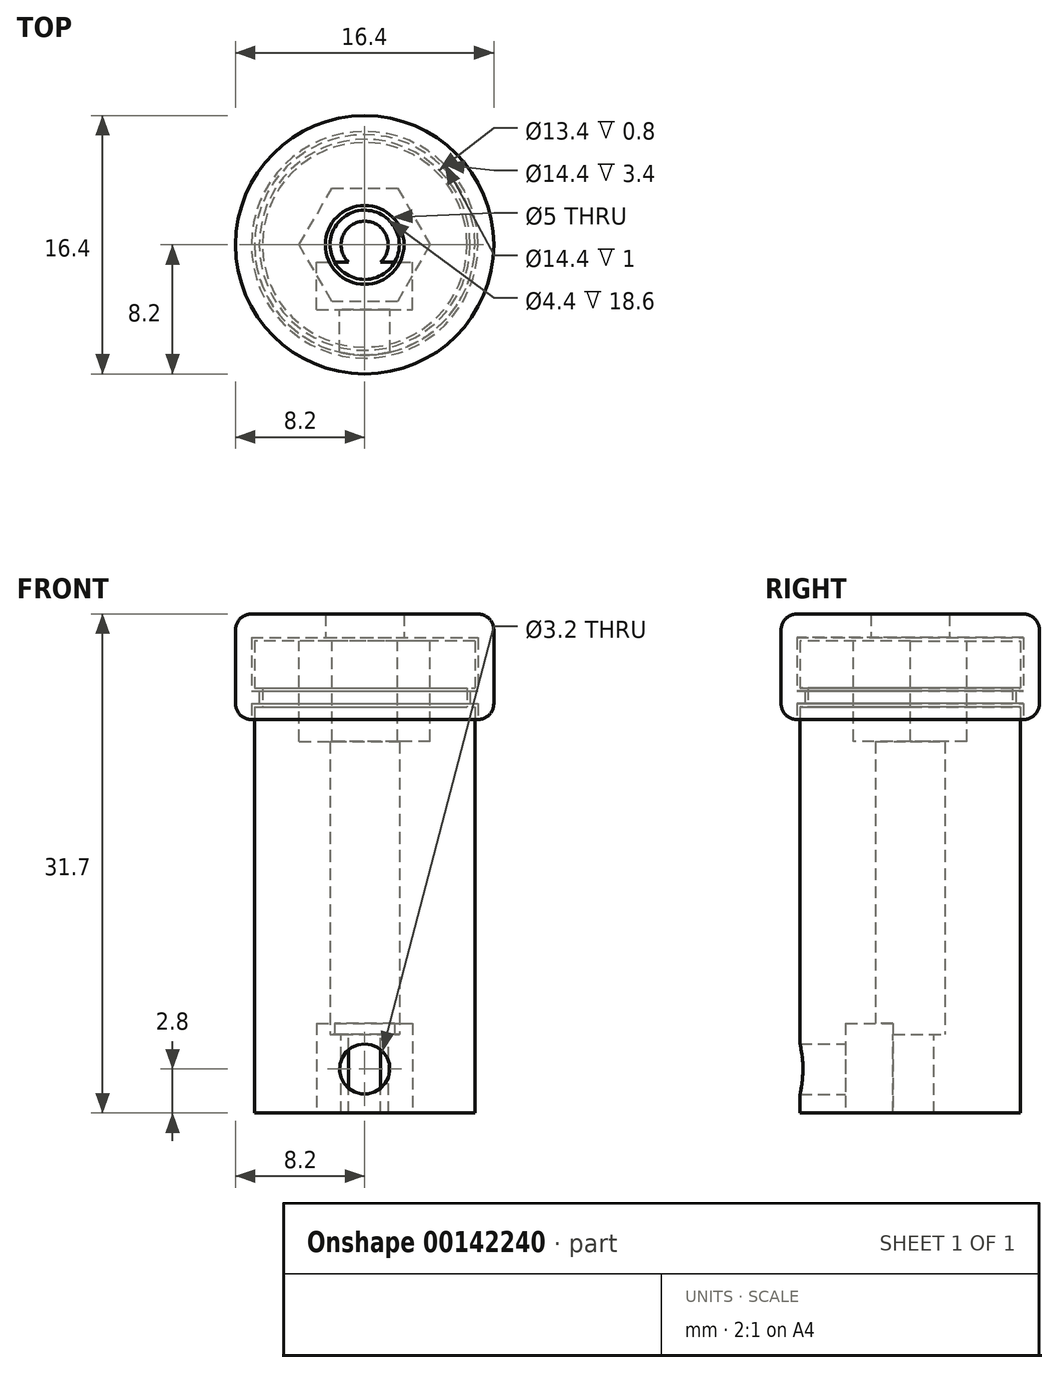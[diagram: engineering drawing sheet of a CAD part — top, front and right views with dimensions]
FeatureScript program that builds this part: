
annotation { "Feature Type Name" : "Feature", "Feature Type Description" : "" }
export const myFeature = defineFeature(function(context is Context, id is Id, definition is map)
    precondition{}
    {
        {
            var Q0;
            Q0=qCreatedBy(makeId("Top.planeOp"),FACE);
            var sketch = newSketch(context, id + "F0", { "sketchPlane" : qUnion([Q0])});
            skCircle(sketch, "E0", {"center": v(0, 0) * mm, "radius": 2.2 * mm});
            skCircle(sketch, "E1", {"center": v(0, 0) * mm, "radius": 7 * mm});
            skSolve(sketch);
        }
        {
            var Q0;
            Q0=makeQuery(id+"F0.imprint","IMPRINT",FACE,{"disambiguationData":[TD([[makeQuery(id+"F0.imprint","IMPRINT",EDGE,{"derivedFrom":sQuery(id+"F0.wireOp",EDGE,"E0")}),-1.0]])]});
            extrude(context, id + "F1", {"entities" : qUnion([Q0]), "depth" : 25 * mm});
        }
        {
            var Q0;
            Q0=makeQuery(id+"F1.opExtrude","CAP_FACE",FACE,{"disambiguationData":[OSD([sQuery(id+"F0.wireOp",EDGE,"E0"),sQuery(id+"F0.wireOp",EDGE,"E1")])],"isStart":false});
            var sketch = newSketch(context, id + "F2", { "sketchPlane" : qUnion([Q0])});
            skCircle(sketch, "E2.cCircle", {"center": v(0, 0) * mm, "radius": 3.6 * mm, "construction": true});
            skLineSegment(sketch, "E2.0", {"start": v(2.08, -3.6) * mm, "end": v(-2.08, -3.6) * mm});
            skLineSegment(sketch, "E2.1", {"start": v(-2.08, -3.6) * mm, "end": v(-4.16, 0) * mm});
            skLineSegment(sketch, "E2.2", {"start": v(-4.16, 0) * mm, "end": v(-2.08, 3.6) * mm});
            skLineSegment(sketch, "E2.3", {"start": v(-2.08, 3.6) * mm, "end": v(2.08, 3.6) * mm});
            skLineSegment(sketch, "E2.4", {"start": v(2.08, 3.6) * mm, "end": v(4.16, 0) * mm});
            skLineSegment(sketch, "E2.5", {"start": v(4.16, 0) * mm, "end": v(2.08, -3.6) * mm});
            skPoint(sketch, "E2.0.midPoint", {"position": v(0, -3.6) * mm});
            skSolve(sketch);
        }
        {
            var Q0;
            Q0=makeQuery(id+"F2.imprint","IMPRINT",FACE,{"disambiguationData":[TD([[makeQuery(id+"F2.imprint","IMPRINT",EDGE,{"derivedFrom":makeQuery(id+"F1.opExtrude","CAP_EDGE",EDGE,{"disambiguationData":[OSD([sQuery(id+"F0.wireOp",EDGE,"E0")])],"isStart":false})}),1.0]])]});
            var Q1;
            Q1=makeQuery(id+"F2.imprint","IMPRINT",FACE,{"disambiguationData":[TD([[makeQuery(id+"F2.imprint","IMPRINT",EDGE,{"derivedFrom":sQuery(id+"F2.wireOp",EDGE,"E2.0")}),-1.0]])]});
            extrude(context, id + "F3", {"entities" : qUnion([Q0, Q1]), "operationType" : NewBodyOperationType.REMOVE, "oppositeDirection" : true, "depth" : 6.4 * mm});
        }
        {
            var Q0;
            Q0=makeQuery(id+"F1.opExtrude","CAP_FACE",FACE,{"disambiguationData":[OSD([sQuery(id+"F0.wireOp",EDGE,"E0"),sQuery(id+"F0.wireOp",EDGE,"E1")])],"isStart":true});
            var sketch = newSketch(context, id + "F4", { "sketchPlane" : qUnion([Q0])});
            skCircle(sketch, "E3", {"center": v(0, 0) * mm, "radius": 1.5 * mm});
            skLineSegment(sketch, "E4", {"start": v(-1.02, 1.1) * mm, "end": v(1.02, 1.1) * mm});
            skCircle(sketch, "E5.0", {"center": v(0, 0) * mm, "radius": 7 * mm});
            skSolve(sketch);
        }
        {
            var Q0;
            Q0 = qSketchRegion(id + "F4", true);
            var Q1;
            Q1=makeQuery(id+"F4.imprint","IMPRINT",FACE,{"disambiguationData":[TD([[makeQuery(id+"F4.imprint","IMPRINT",EDGE,{"derivedFrom":sQuery(id+"F4.wireOp",EDGE,"E5.0")}),-1.0]])]});
            var Q2;
            {var subQ0=sQuery(id+"F4.wireOp",EDGE,"E4");Q2=makeQuery(id+"F4.imprint","IMPRINT",FACE,{"disambiguationData":[TD([[makeQuery(id+"F4.imprint","IMPRINT",EDGE,{"derivedFrom":subQ0}),1.0]])]});}
            extrude(context, id + "F5", {"entities" : qUnion([Q0, Q1, Q2]), "operationType" : NewBodyOperationType.ADD, "depth" : 5 * mm});
        }
        {
            var Q0;
            Q0=qCreatedBy(makeId("Front.planeOp"),FACE);
            var sketch = newSketch(context, id + "F6", { "sketchPlane" : qUnion([Q0])});
            skLineSegment(sketch, "E6", {"start": v(-7, -5) * mm, "end": v(-7, 24.85) * mm});
            skLineSegment(sketch, "E7", {"start": v(7, 25) * mm, "end": v(7, -5) * mm});
            skLineSegment(sketch, "E8.bottom", {"start": v(-7, 22) * mm, "end": v(-6.5, 22) * mm});
            skLineSegment(sketch, "E8.top", {"start": v(-7, 20.8) * mm, "end": v(-6.5, 20.8) * mm});
            skLineSegment(sketch, "E8.left", {"start": v(-7, 22) * mm, "end": v(-7, 20.8) * mm});
            skLineSegment(sketch, "E8.right", {"start": v(-6.5, 22) * mm, "end": v(-6.5, 20.8) * mm});
            skSolve(sketch);
        }
        {
            var Q0;
            Q0 = qSketchRegion(id + "F6", true);
            var Q1;
            Q1=makeQuery(id+"F1.opExtrude","CAP_EDGE",EDGE,{"disambiguationData":[OSD([sQuery(id+"F0.wireOp",EDGE,"E1")])],"isStart":false});
            revolve(context, id + "F7", {"operationType" : NewBodyOperationType.REMOVE, "entities" : qUnion([Q0]), "axis" : qUnion([Q1]), "revolveType" : RevolveType.FULL});
        }
        {
            var Q0;
            Q0=qCreatedBy(makeId("Front.planeOp"),FACE);
            var sketch = newSketch(context, id + "F8", { "sketchPlane" : qUnion([Q0])});
            skLineSegment(sketch, "E9", {"start": v(-7, 22) * mm, "end": v(-7, 25) * mm, "construction": true});
            skLineSegment(sketch, "E10", {"start": v(-6.5, 20.8) * mm, "end": v(-6.5, 22) * mm, "construction": true});
            skLineSegment(sketch, "E11.0", {"start": v(-7, 25) * mm, "end": v(7, 25) * mm, "construction": true});
            skLineSegment(sketch, "E12", {"start": v(-6.5, 22) * mm, "end": v(-7, 22) * mm});
            skLineSegment(sketch, "E13.0", {"start": v(-7.2, 25.2) * mm, "end": v(5, 25.2) * mm});
            skLineSegment(sketch, "E13.1", {"start": v(-7.2, 21.8) * mm, "end": v(-7.2, 25.2) * mm});
            skLineSegment(sketch, "E13.3", {"start": v(-6.7, 21) * mm, "end": v(-7.2, 21) * mm});
            skLineSegment(sketch, "E13.4", {"start": v(-6.7, 21) * mm, "end": v(-6.7, 21.8) * mm});
            skLineSegment(sketch, "E13.5", {"start": v(-6.7, 21.8) * mm, "end": v(-7.2, 21.8) * mm});
            skLineSegment(sketch, "E14", {"start": v(-7.2, 21) * mm, "end": v(-7.2, 20) * mm});
            skLineSegment(sketch, "E15", {"start": v(-7, -5) * mm, "end": v(-7, 20.8) * mm, "construction": true});
            skLineSegment(sketch, "E16.0", {"start": v(7, 20.8) * mm, "end": v(-7, 20.8) * mm, "construction": true});
            skLineSegment(sketch, "E17", {"start": v(-7.2, 20) * mm, "end": v(-8.2, 20) * mm});
            skLineSegment(sketch, "E18", {"start": v(-8.2, 20) * mm, "end": v(-8.2, 26.7) * mm});
            skLineSegment(sketch, "E19", {"start": v(-8.2, 26.7) * mm, "end": v(0, 26.7) * mm});
            skLineSegment(sketch, "E20", {"start": v(-2.5, 25.2) * mm, "end": v(-2.5, 26.7) * mm});
            skSolve(sketch);
        }
        {
            var Q0;
            {var subQ0=sQuery(id+"F8.wireOp",EDGE,"E13.1");Q0=makeQuery(id+"F8.imprint","IMPRINT",FACE,{"disambiguationData":[TD([[makeQuery(id+"F8.imprint","IMPRINT",EDGE,{"derivedFrom":subQ0}),1.0]])]});}
            var Q1;
            Q1=makeQuery(id+"F1.opExtrude","CAP_EDGE",EDGE,{"disambiguationData":[OSD([sQuery(id+"F0.wireOp",EDGE,"E1")])],"isStart":false});
            revolve(context, id + "F9", {"entities" : qUnion([Q0]), "axis" : qUnion([Q1]), "revolveType" : RevolveType.FULL});
        }
        {
            var Q0;
            Q0=makeQuery(id+"F9.opRevolve","SWEPT_EDGE",EDGE,{"disambiguationData":[OSD([sQuery(id+"F8.wireOp",EDGE,"E17"),sQuery(id+"F8.wireOp",EDGE,"E18")])]});
            var Q1;
            Q1=makeQuery(id+"F9.opRevolve","SWEPT_EDGE",EDGE,{"disambiguationData":[OSD([sQuery(id+"F8.wireOp",EDGE,"E18"),sQuery(id+"F8.wireOp",EDGE,"E19")])]});
            fillet(context, id + "F10", {"entities" : qUnion([Q0, Q1]), "radius" : 1 * mm, "tangentPropagation" : true, "allowEdgeOverflow" : false});
        }
        {
            var Q0;
            Q0=makeQuery(id+"F5.opExtrude","CAP_FACE",FACE,{"disambiguationData":[OSD([sQuery(id+"F4.wireOp",EDGE,"E3"),sQuery(id+"F4.wireOp",EDGE,"E4"),sQuery(id+"F4.wireOp",EDGE,"E5.0")])],"isStart":false});
            var sketch = newSketch(context, id + "F11", { "sketchPlane" : qUnion([Q0])});
            skLineSegment(sketch, "E21.bottom", {"start": v(-3.05, 4.1) * mm, "end": v(3.05, 4.1) * mm});
            skLineSegment(sketch, "E21.top", {"start": v(-3.05, 1.1) * mm, "end": v(3.05, 1.1) * mm});
            skLineSegment(sketch, "E21.left", {"start": v(-3.05, 4.1) * mm, "end": v(-3.05, 1.1) * mm});
            skLineSegment(sketch, "E21.right", {"start": v(3.05, 4.1) * mm, "end": v(3.05, 1.1) * mm});
            skSolve(sketch);
        }
        {
            var Q0;
            Q0=makeQuery(id+"F11.imprint","IMPRINT",FACE,{"disambiguationData":[TD([[makeQuery(id+"F11.imprint","IMPRINT",EDGE,{"derivedFrom":sQuery(id+"F11.wireOp",EDGE,"E21.bottom")}),-1.0]])]});
            extrude(context, id + "F12", {"entities" : qUnion([Q0]), "operationType" : NewBodyOperationType.REMOVE, "oppositeDirection" : true, "depth" : 5.7 * mm});
        }
        {
            var Q0;
            Q0=makeQuery(id+"F12.boolean.opBoolean","COPY",FACE,{"derivedFrom":makeQuery(id+"F12.opExtrude","SWEPT_FACE",FACE,{"disambiguationData":[OSD([sQuery(id+"F11.wireOp",EDGE,"E21.bottom")])]})});
            var sketch = newSketch(context, id + "F13", { "sketchPlane" : qUnion([Q0])});
            skCircle(sketch, "E22", {"center": v(0, -2.2) * mm, "radius": 1.6 * mm});
            skSolve(sketch);
        }
        {
            var Q0;
            Q0=makeQuery(id+"F13.imprint","IMPRINT",FACE,{"disambiguationData":[TD([[makeQuery(id+"F13.imprint","IMPRINT",EDGE,{"derivedFrom":sQuery(id+"F13.wireOp",EDGE,"E22")}),1.0]])]});
            extrude(context, id + "F14", {"entities" : qUnion([Q0]), "operationType" : NewBodyOperationType.REMOVE, "endBound" : BoundingType.THROUGH_ALL, "oppositeDirection" : true, "depth" : 25 * mm});
        }
    });
